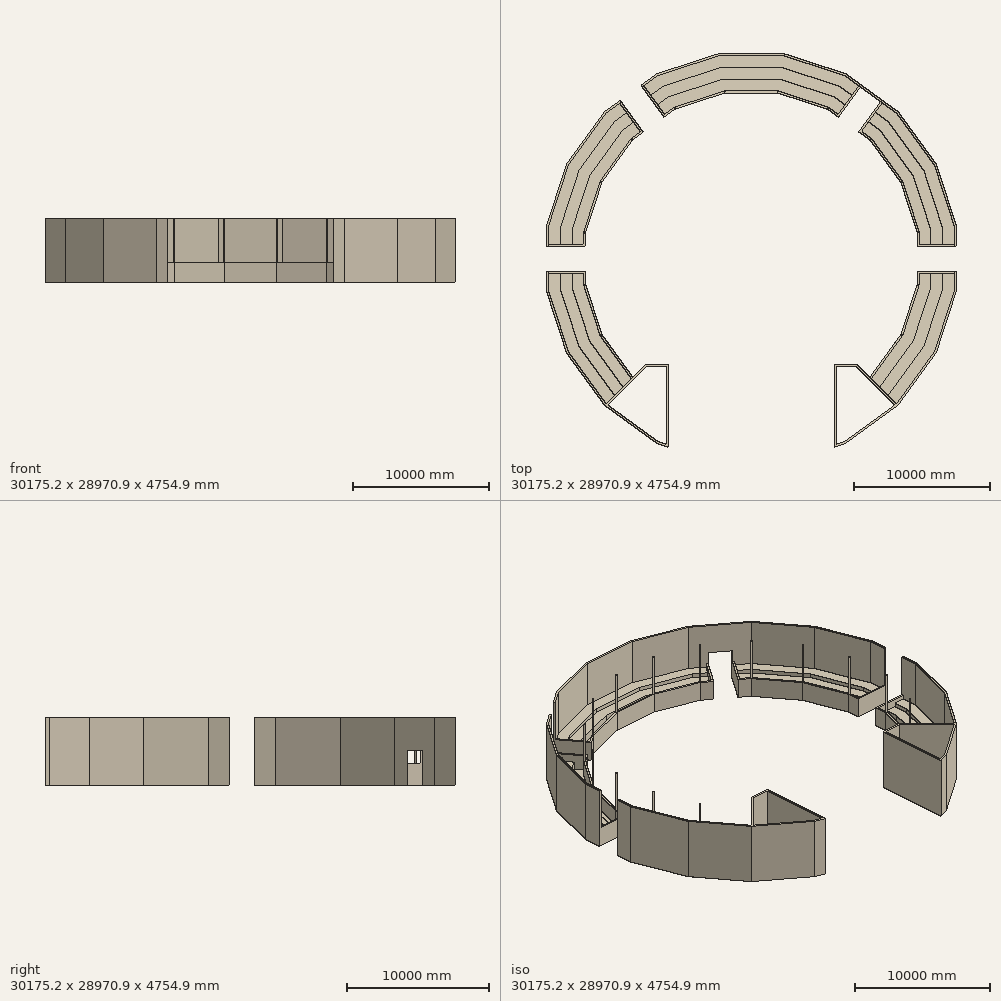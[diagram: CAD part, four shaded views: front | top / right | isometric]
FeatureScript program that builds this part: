
annotation { "Feature Type Name" : "Feature", "Feature Type Description" : "" }
export const myFeature = defineFeature(function(context is Context, id is Id, definition is map)
    precondition{}
    {
        {
            var Q0;
            Q0=qCreatedBy(makeId("Top.planeOp"),FACE);
            var sketch = newSketch(context, id + "F0", { "sketchPlane" : qUnion([Q0])});
            skLineSegment(sketch, "E0.0", {"start": v(-2389.64, 15087.6) * mm, "end": v(2389.64, 15087.6) * mm});
            skLineSegment(sketch, "E0.1", {"start": v(2389.64, 15087.6) * mm, "end": v(6935, 13610.72) * mm});
            skLineSegment(sketch, "E0.2", {"start": v(6935, 13610.72) * mm, "end": v(10801.53, 10801.53) * mm});
            skLineSegment(sketch, "E0.3", {"start": v(10801.53, 10801.53) * mm, "end": v(13610.72, 6935) * mm});
            skLineSegment(sketch, "E0.4", {"start": v(13610.72, 6935) * mm, "end": v(15087.6, 2389.64) * mm});
            skLineSegment(sketch, "E0.5", {"start": v(15087.6, 2389.64) * mm, "end": v(15087.6, -2389.64) * mm});
            skLineSegment(sketch, "E0.6", {"start": v(15087.6, -2389.64) * mm, "end": v(13610.72, -6935) * mm});
            skLineSegment(sketch, "E0.7", {"start": v(13610.72, -6935) * mm, "end": v(10801.53, -10801.53) * mm});
            skLineSegment(sketch, "E0.8", {"start": v(10801.53, -10801.53) * mm, "end": v(6935, -13610.72) * mm});
            skLineSegment(sketch, "E0.9", {"start": v(6935, -13610.72) * mm, "end": v(2389.64, -15087.6) * mm});
            skLineSegment(sketch, "E0.10", {"start": v(2389.64, -15087.6) * mm, "end": v(-2389.64, -15087.6) * mm});
            skLineSegment(sketch, "E0.11", {"start": v(-2389.64, -15087.6) * mm, "end": v(-6935, -13610.72) * mm});
            skLineSegment(sketch, "E0.12", {"start": v(-6935, -13610.72) * mm, "end": v(-10801.53, -10801.53) * mm});
            skLineSegment(sketch, "E0.13", {"start": v(-10801.53, -10801.53) * mm, "end": v(-13610.72, -6935) * mm});
            skLineSegment(sketch, "E0.14", {"start": v(-13610.72, -6935) * mm, "end": v(-15087.6, -2389.64) * mm});
            skLineSegment(sketch, "E0.15", {"start": v(-15087.6, -2389.64) * mm, "end": v(-15087.6, 2389.64) * mm});
            skLineSegment(sketch, "E0.16", {"start": v(-15087.6, 2389.64) * mm, "end": v(-13610.72, 6935) * mm});
            skLineSegment(sketch, "E0.17", {"start": v(-13610.72, 6935) * mm, "end": v(-10801.53, 10801.53) * mm});
            skLineSegment(sketch, "E0.18", {"start": v(-10801.53, 10801.53) * mm, "end": v(-6935, 13610.72) * mm});
            skLineSegment(sketch, "E0.19", {"start": v(-6935, 13610.72) * mm, "end": v(-2389.64, 15087.6) * mm});
            skLineSegment(sketch, "E1", {"start": v(-6705.6, -7772.4) * mm, "end": v(-6705.6, -152.4) * mm});
            skLineSegment(sketch, "E2", {"start": v(-6705.6, -152.4) * mm, "end": v(6705.6, -152.4) * mm});
            skLineSegment(sketch, "E3", {"start": v(6705.6, -152.4) * mm, "end": v(6705.6, -7772.4) * mm});
            skLineSegment(sketch, "E4", {"start": v(-6096, -7772.4) * mm, "end": v(-6096, -13883.33) * mm});
            skLineSegment(sketch, "E5", {"start": v(6096, -7772.4) * mm, "end": v(6096, -13883.33) * mm});
            skLineSegment(sketch, "E6", {"start": v(-7772.4, -7772.4) * mm, "end": v(-6096, -7772.4) * mm});
            skLineSegment(sketch, "E7", {"start": v(6096, -7772.4) * mm, "end": v(6705.6, -7772.4) * mm});
            skPoint(sketch, "E8.startSnap0", {"position": v(0, -15087.6) * mm});
            skLineSegment(sketch, "E9.0", {"start": v(-1931.02, 12192) * mm, "end": v(1931.02, 12192) * mm});
            skLineSegment(sketch, "E9.1", {"start": v(1931.02, 12192) * mm, "end": v(5604.05, 10998.56) * mm});
            skLineSegment(sketch, "E9.2", {"start": v(5604.05, 10998.56) * mm, "end": v(6426.51, 10401) * mm});
            skLineSegment(sketch, "E9.3", {"start": v(8728.5, 8728.5) * mm, "end": v(10998.56, 5604.05) * mm});
            skLineSegment(sketch, "E9.4", {"start": v(10998.56, 5604.05) * mm, "end": v(12192, 1931.02) * mm});
            skLineSegment(sketch, "E9.5", {"start": v(12192, 1931.02) * mm, "end": v(12192, 914.4) * mm});
            skLineSegment(sketch, "E9.6", {"start": v(12192, -1931.02) * mm, "end": v(10998.56, -5604.05) * mm});
            skLineSegment(sketch, "E9.13", {"start": v(-8728.5, -8728.5) * mm, "end": v(-10998.56, -5604.05) * mm});
            skLineSegment(sketch, "E9.14", {"start": v(-10998.56, -5604.05) * mm, "end": v(-12192, -1931.02) * mm});
            skLineSegment(sketch, "E9.15", {"start": v(-12192, -1931.02) * mm, "end": v(-12192, -914.4) * mm});
            skLineSegment(sketch, "E9.16", {"start": v(-12192, 1931.02) * mm, "end": v(-10998.56, 5604.05) * mm});
            skLineSegment(sketch, "E9.17", {"start": v(-10998.56, 5604.05) * mm, "end": v(-8728.5, 8728.5) * mm});
            skLineSegment(sketch, "E9.18", {"start": v(-8728.5, 8728.5) * mm, "end": v(-7953.14, 9291.85) * mm});
            skLineSegment(sketch, "E9.19", {"start": v(-5604.05, 10998.56) * mm, "end": v(-1931.02, 12192) * mm});
            skLineSegment(sketch, "E10", {"start": v(-15087.6, 0) * mm, "end": v(-15087.6, 914.4) * mm});
            skLineSegment(sketch, "E11", {"start": v(-14935.2, 914.4) * mm, "end": v(-12192, 914.4) * mm});
            skPoint(sketch, "E11.endSnap0", {"position": v(15087.6, 0) * mm});
            skLineSegment(sketch, "E12", {"start": v(15087.6, 914.4) * mm, "end": v(15087.6, -914.4) * mm});
            skLineSegment(sketch, "E13", {"start": v(14935.2, -914.4) * mm, "end": v(12192, -914.4) * mm});
            skLineSegment(sketch, "E14.trimOffspring", {"start": v(12192, 914.4) * mm, "end": v(14935.2, 914.4) * mm});
            skLineSegment(sketch, "E15.trimOffspring", {"start": v(-12192, -914.4) * mm, "end": v(-14935.2, -914.4) * mm});
            skLineSegment(sketch, "E16.trimOffspring", {"start": v(-12192, 914.4) * mm, "end": v(-12192, 1931.02) * mm});
            skLineSegment(sketch, "E17.trimOffspring", {"start": v(12192, -914.4) * mm, "end": v(12192, -1931.02) * mm});
            skLineSegment(sketch, "E18", {"start": v(-7953.14, 9291.85) * mm, "end": v(-9565.55, 11511.14) * mm});
            skLineSegment(sketch, "E19", {"start": v(-9655.13, 11634.44) * mm, "end": v(-8128.5, 12743.6) * mm});
            skLineSegment(sketch, "E20", {"start": v(-8038.93, 12620.3) * mm, "end": v(-6426.51, 10401) * mm});
            skLineSegment(sketch, "E21.trimOffspring", {"start": v(-6426.51, 10401) * mm, "end": v(-5604.05, 10998.56) * mm});
            skLineSegment(sketch, "E22.MirrorCS", {"start": v(8038.93, 12620.3) * mm, "end": v(6426.51, 10401) * mm});
            skLineSegment(sketch, "E23.MirrorCS", {"start": v(7906.04, 9326.06) * mm, "end": v(9518.46, 11545.36) * mm});
            skLineSegment(sketch, "E24.trimOffspring", {"start": v(7906.04, 9326.06) * mm, "end": v(8728.5, 8728.5) * mm});
            skLineSegment(sketch, "E25.0", {"start": v(-2365.5, 14935.2) * mm, "end": v(2365.5, 14935.2) * mm});
            skLineSegment(sketch, "E25.1", {"start": v(2365.5, 14935.2) * mm, "end": v(6864.96, 13473.24) * mm});
            skLineSegment(sketch, "E25.2", {"start": v(6864.96, 13473.24) * mm, "end": v(7915.63, 12709.88) * mm});
            skLineSegment(sketch, "E25.3", {"start": v(10692.42, 10692.42) * mm, "end": v(13473.24, 6864.96) * mm});
            skLineSegment(sketch, "E25.4", {"start": v(13473.24, 6864.96) * mm, "end": v(14935.2, 2365.5) * mm});
            skLineSegment(sketch, "E25.5", {"start": v(14935.2, 2365.5) * mm, "end": v(14935.2, 1066.8) * mm});
            skLineSegment(sketch, "E25.6", {"start": v(14935.2, -2365.5) * mm, "end": v(13473.24, -6864.96) * mm});
            skLineSegment(sketch, "E25.12", {"start": v(-6864.96, -13473.24) * mm, "end": v(-10567.6, -10783.12) * mm});
            skLineSegment(sketch, "E25.13", {"start": v(-10692.42, -10692.42) * mm, "end": v(-13473.24, -6864.96) * mm});
            skLineSegment(sketch, "E25.14", {"start": v(-13473.24, -6864.96) * mm, "end": v(-14935.2, -2365.5) * mm});
            skLineSegment(sketch, "E25.15", {"start": v(-14935.2, -2365.5) * mm, "end": v(-14935.2, -1066.8) * mm});
            skLineSegment(sketch, "E25.16", {"start": v(-14935.2, 2365.5) * mm, "end": v(-13473.24, 6864.96) * mm});
            skLineSegment(sketch, "E25.17", {"start": v(-13473.24, 6864.96) * mm, "end": v(-10692.42, 10692.42) * mm});
            skLineSegment(sketch, "E25.18", {"start": v(-10692.42, 10692.42) * mm, "end": v(-9688.84, 11421.57) * mm});
            skLineSegment(sketch, "E25.19", {"start": v(-6864.96, 13473.24) * mm, "end": v(-2365.5, 14935.2) * mm});
            skLineSegment(sketch, "E26.trimOffspring", {"start": v(-7915.63, 12709.88) * mm, "end": v(-6864.96, 13473.24) * mm});
            skLineSegment(sketch, "E27", {"start": v(0, 12192) * mm, "end": v(0, 12344.4) * mm});
            skLineSegment(sketch, "E28.0", {"start": v(-1955.16, 12344.4) * mm, "end": v(1955.16, 12344.4) * mm});
            skLineSegment(sketch, "E28.1", {"start": v(1955.16, 12344.4) * mm, "end": v(5674.1, 11136.04) * mm});
            skLineSegment(sketch, "E28.2", {"start": v(5674.1, 11136.04) * mm, "end": v(6392.8, 10613.88) * mm});
            skLineSegment(sketch, "E28.3", {"start": v(8837.61, 8837.61) * mm, "end": v(11136.04, 5674.1) * mm});
            skLineSegment(sketch, "E28.4", {"start": v(11136.04, 5674.1) * mm, "end": v(12344.4, 1955.16) * mm});
            skLineSegment(sketch, "E28.5", {"start": v(12344.4, 1955.16) * mm, "end": v(12344.4, 1066.8) * mm});
            skLineSegment(sketch, "E28.6", {"start": v(12344.4, -1955.16) * mm, "end": v(11136.04, -5674.1) * mm});
            skLineSegment(sketch, "E28.13", {"start": v(-8837.61, -8837.61) * mm, "end": v(-11136.04, -5674.1) * mm});
            skLineSegment(sketch, "E28.14", {"start": v(-11136.04, -5674.1) * mm, "end": v(-12344.4, -1955.16) * mm});
            skLineSegment(sketch, "E28.15", {"start": v(-12344.4, -1955.16) * mm, "end": v(-12344.4, -1066.8) * mm});
            skLineSegment(sketch, "E28.16", {"start": v(-12344.4, 1955.16) * mm, "end": v(-11136.04, 5674.1) * mm});
            skLineSegment(sketch, "E28.17", {"start": v(-11136.04, 5674.1) * mm, "end": v(-8837.61, 8837.61) * mm});
            skLineSegment(sketch, "E28.18", {"start": v(-8837.61, 8837.61) * mm, "end": v(-8166, 9325.56) * mm});
            skLineSegment(sketch, "E28.19", {"start": v(-5674.1, 11136.04) * mm, "end": v(-1955.16, 12344.4) * mm});
            skPoint(sketch, "E28.0.midPoint", {"position": v(0, 12344.4) * mm});
            skLineSegment(sketch, "E29.trimOffspring", {"start": v(-6392.8, 10613.88) * mm, "end": v(-5674.1, 11136.04) * mm});
            skLineSegment(sketch, "E30.trimOffspring", {"start": v(8118.92, 9359.78) * mm, "end": v(8837.61, 8837.61) * mm});
            skLineSegment(sketch, "E31", {"start": v(-10692.42, -10692.42) * mm, "end": v(-7772.4, -7772.4) * mm});
            skLineSegment(sketch, "E32", {"start": v(-8837.61, -8837.61) * mm, "end": v(-10692.42, -10692.42) * mm});
            skLineSegment(sketch, "E33", {"start": v(-7709.27, -7924.8) * mm, "end": v(-10567.6, -10783.12) * mm});
            skLineSegment(sketch, "E34", {"start": v(-6096, -7772.4) * mm, "end": v(-6096, -7924.8) * mm});
            skLineSegment(sketch, "E35", {"start": v(-6248.4, -7924.8) * mm, "end": v(-7709.27, -7924.8) * mm});
            skPoint(sketch, "E36.orphan", {"position": v(-7556.87, -7772.4) * mm});
            skLineSegment(sketch, "E37", {"start": v(-6248.4, -7924.8) * mm, "end": v(-6248.4, -13673.57) * mm});
            skLineSegment(sketch, "E38.trimOffspring", {"start": v(-6248.4, -13673.57) * mm, "end": v(-6864.96, -13473.24) * mm});
            skLineSegment(sketch, "E39.MirrorCS", {"start": v(8728.5, -8728.5) * mm, "end": v(10998.56, -5604.05) * mm});
            skLineSegment(sketch, "E40.MirrorCS", {"start": v(7709.27, -7924.8) * mm, "end": v(10567.6, -10783.12) * mm});
            skLineSegment(sketch, "E41.MirrorCS", {"start": v(6248.4, -7924.8) * mm, "end": v(7709.27, -7924.8) * mm});
            skLineSegment(sketch, "E42.MirrorCS", {"start": v(7772.4, -7772.4) * mm, "end": v(6096, -7772.4) * mm});
            skPoint(sketch, "E43.MirrorP", {"position": v(7556.87, -7772.4) * mm});
            skLineSegment(sketch, "E44.MirrorCS", {"start": v(8837.61, -8837.61) * mm, "end": v(11136.04, -5674.1) * mm});
            skLineSegment(sketch, "E45.MirrorCS", {"start": v(10692.42, -10692.42) * mm, "end": v(7772.4, -7772.4) * mm});
            skLineSegment(sketch, "E46.MirrorCS", {"start": v(8837.61, -8837.61) * mm, "end": v(10692.42, -10692.42) * mm});
            skLineSegment(sketch, "E47.MirrorCS", {"start": v(6864.96, -13473.24) * mm, "end": v(10567.6, -10783.12) * mm});
            skLineSegment(sketch, "E48.MirrorCS", {"start": v(10692.42, -10692.42) * mm, "end": v(13473.24, -6864.96) * mm});
            skLineSegment(sketch, "E49.MirrorCS", {"start": v(6248.4, -13673.57) * mm, "end": v(6864.96, -13473.24) * mm});
            skLineSegment(sketch, "E50.MirrorCS", {"start": v(6248.4, -7924.8) * mm, "end": v(6248.4, -13673.57) * mm});
            skLineSegment(sketch, "E51.trimOffspring", {"start": v(-12344.4, 1066.8) * mm, "end": v(-12344.4, 1955.16) * mm});
            skLineSegment(sketch, "E52.trimOffspring", {"start": v(-14935.2, 1066.8) * mm, "end": v(-14935.2, 2365.5) * mm});
            skLineSegment(sketch, "E53", {"start": v(-14935.2, -1066.8) * mm, "end": v(-12344.4, -1066.8) * mm});
            skLineSegment(sketch, "E54.0", {"start": v(-14071.6, -2228.72) * mm, "end": v(-14071.6, -1066.8) * mm});
            skLineSegment(sketch, "E54.1", {"start": v(-14071.6, 2228.72) * mm, "end": v(-12694.17, 6468) * mm});
            skLineSegment(sketch, "E54.2", {"start": v(-12694.17, 6468) * mm, "end": v(-10074.15, 10074.15) * mm});
            skLineSegment(sketch, "E54.3", {"start": v(-10074.15, 10074.15) * mm, "end": v(-9181.23, 10722.9) * mm});
            skLineSegment(sketch, "E54.4", {"start": v(-6468, 12694.17) * mm, "end": v(-2228.72, 14071.6) * mm});
            skLineSegment(sketch, "E54.5", {"start": v(-2228.72, 14071.6) * mm, "end": v(2228.72, 14071.6) * mm});
            skLineSegment(sketch, "E54.6", {"start": v(2228.72, 14071.6) * mm, "end": v(6468, 12694.17) * mm});
            skLineSegment(sketch, "E54.7", {"start": v(6468, 12694.17) * mm, "end": v(7408.02, 12011.21) * mm});
            skLineSegment(sketch, "E54.8", {"start": v(10074.15, 10074.15) * mm, "end": v(12694.17, 6468) * mm});
            skLineSegment(sketch, "E54.9", {"start": v(12694.17, 6468) * mm, "end": v(14071.6, 2228.72) * mm});
            skLineSegment(sketch, "E54.10", {"start": v(14071.6, 2228.72) * mm, "end": v(14071.6, 1066.8) * mm});
            skLineSegment(sketch, "E54.11", {"start": v(14071.6, -2228.72) * mm, "end": v(12694.17, -6468) * mm});
            skLineSegment(sketch, "E54.12", {"start": v(12694.17, -6468) * mm, "end": v(10074.15, -10074.15) * mm});
            skLineSegment(sketch, "E54.18", {"start": v(-10074.15, -10074.15) * mm, "end": v(-12694.17, -6468) * mm});
            skLineSegment(sketch, "E54.19", {"start": v(-12694.17, -6468) * mm, "end": v(-14071.6, -2228.72) * mm});
            skLineSegment(sketch, "E55.0", {"start": v(-13208, -2091.94) * mm, "end": v(-13208, -1066.8) * mm});
            skLineSegment(sketch, "E55.1", {"start": v(-13208, 2091.94) * mm, "end": v(-11915.1, 6071.05) * mm});
            skLineSegment(sketch, "E55.2", {"start": v(-11915.1, 6071.05) * mm, "end": v(-9455.88, 9455.88) * mm});
            skLineSegment(sketch, "E55.3", {"start": v(-9455.88, 9455.88) * mm, "end": v(-8673.62, 10024.23) * mm});
            skLineSegment(sketch, "E55.4", {"start": v(-6071.05, 11915.1) * mm, "end": v(-2091.94, 13208) * mm});
            skLineSegment(sketch, "E55.5", {"start": v(-2091.94, 13208) * mm, "end": v(2091.94, 13208) * mm});
            skLineSegment(sketch, "E55.6", {"start": v(2091.94, 13208) * mm, "end": v(6071.05, 11915.1) * mm});
            skLineSegment(sketch, "E55.8", {"start": v(9455.88, 9455.88) * mm, "end": v(11915.1, 6071.05) * mm});
            skLineSegment(sketch, "E55.9", {"start": v(11915.1, 6071.05) * mm, "end": v(13208, 2091.94) * mm});
            skLineSegment(sketch, "E55.10", {"start": v(13208, 2091.94) * mm, "end": v(13208, 1066.8) * mm});
            skLineSegment(sketch, "E55.11", {"start": v(13208, -2091.94) * mm, "end": v(11915.1, -6071.05) * mm});
            skLineSegment(sketch, "E55.12", {"start": v(11915.1, -6071.05) * mm, "end": v(9455.88, -9455.88) * mm});
            skLineSegment(sketch, "E55.18", {"start": v(-9455.88, -9455.88) * mm, "end": v(-11915.1, -6071.05) * mm});
            skLineSegment(sketch, "E55.19", {"start": v(-11915.1, -6071.05) * mm, "end": v(-13208, -2091.94) * mm});
            skLineSegment(sketch, "E56.trimOffspring", {"start": v(-14071.6, 1066.8) * mm, "end": v(-14071.6, 2228.72) * mm});
            skLineSegment(sketch, "E57", {"start": v(-13208, 2091.94) * mm, "end": v(-13208, 1066.8) * mm});
            skLineSegment(sketch, "E58", {"start": v(-14935.2, 1066.8) * mm, "end": v(-12344.4, 1066.8) * mm});
            skLineSegment(sketch, "E59", {"start": v(-9688.84, 11421.57) * mm, "end": v(-8166, 9325.56) * mm});
            skLineSegment(sketch, "E60", {"start": v(-7915.63, 12709.88) * mm, "end": v(-6392.8, 10613.88) * mm});
            skLineSegment(sketch, "E61.trimOffspring", {"start": v(-7408.02, 12011.21) * mm, "end": v(-6468, 12694.17) * mm});
            skLineSegment(sketch, "E62.trimOffspring", {"start": v(-6900.4, 11312.55) * mm, "end": v(-6071.05, 11915.1) * mm});
            skLineSegment(sketch, "E63", {"start": v(6392.8, 10613.88) * mm, "end": v(7915.63, 12709.88) * mm});
            skLineSegment(sketch, "E64.trimOffspring", {"start": v(9134.14, 10757.11) * mm, "end": v(10074.15, 10074.15) * mm});
            skLineSegment(sketch, "E65.trimOffspring", {"start": v(8626.53, 10058.45) * mm, "end": v(9455.88, 9455.88) * mm});
            skLineSegment(sketch, "E66.trimOffspring", {"start": v(9641.75, 11455.78) * mm, "end": v(10692.42, 10692.42) * mm});
            skLineSegment(sketch, "E67", {"start": v(8118.92, 9359.78) * mm, "end": v(9641.75, 11455.78) * mm});
            skLineSegment(sketch, "E68", {"start": v(6071.05, 11915.1) * mm, "end": v(6900.4, 11312.55) * mm});
            skLineSegment(sketch, "E69.trimOffspring", {"start": v(12344.4, -1066.8) * mm, "end": v(12344.4, -1955.16) * mm});
            skLineSegment(sketch, "E70.trimOffspring", {"start": v(13208, -1066.8) * mm, "end": v(13208, -2091.94) * mm});
            skLineSegment(sketch, "E71.trimOffspring", {"start": v(14071.6, -1066.8) * mm, "end": v(14071.6, -2228.72) * mm});
            skLineSegment(sketch, "E72", {"start": v(12344.4, 1066.8) * mm, "end": v(14935.2, 1066.8) * mm});
            skLineSegment(sketch, "E73", {"start": v(12344.4, -1066.8) * mm, "end": v(14935.2, -1066.8) * mm});
            skLineSegment(sketch, "E74.trimOffspring", {"start": v(14935.2, -1066.8) * mm, "end": v(14935.2, -2365.5) * mm});
            skLineSegment(sketch, "E75", {"start": v(-8038.93, 12620.3) * mm, "end": v(-9565.55, 11511.14) * mm});
            skLineSegment(sketch, "E76", {"start": v(8038.93, 12620.3) * mm, "end": v(9518.46, 11545.36) * mm});
            skLineSegment(sketch, "E77", {"start": v(14935.2, -914.4) * mm, "end": v(14935.2, 914.4) * mm});
            skLineSegment(sketch, "E78", {"start": v(-14935.2, 914.4) * mm, "end": v(-14935.2, -914.4) * mm});
            skLineSegment(sketch, "E79", {"start": v(-14935.2, -914.4) * mm, "end": v(-14935.2, -1066.8) * mm});
            skLineSegment(sketch, "E80", {"start": v(-14935.2, 1066.8) * mm, "end": v(-14935.2, 914.4) * mm});
            skLineSegment(sketch, "E81", {"start": v(-9565.55, 11511.14) * mm, "end": v(-9688.84, 11421.57) * mm});
            skLineSegment(sketch, "E82", {"start": v(-8038.93, 12620.3) * mm, "end": v(-7915.63, 12709.88) * mm});
            skLineSegment(sketch, "E83", {"start": v(7915.63, 12709.88) * mm, "end": v(8038.93, 12620.3) * mm});
            skLineSegment(sketch, "E84", {"start": v(9518.46, 11545.36) * mm, "end": v(9641.75, 11455.78) * mm});
            skLineSegment(sketch, "E85", {"start": v(14935.2, -914.4) * mm, "end": v(14935.2, -1066.8) * mm});
            skLineSegment(sketch, "E86", {"start": v(14935.2, 1066.8) * mm, "end": v(14935.2, 914.4) * mm});
            skPoint(sketch, "E87.center", {"position": v(0, 0) * mm});
            skCircle(sketch, "E88", {"center": v(-11067.3, -5639.07) * mm, "radius": 60.96 * mm});
            skCircle(sketch, "E89.7.0", {"center": v(11067.3, -5639.07) * mm, "radius": 60.96 * mm});
            skCircle(sketch, "E89.8.0", {"center": v(12268.2, -1943.1) * mm, "radius": 60.96 * mm});
            skCircle(sketch, "E89.9.0", {"center": v(12268.2, 1943.1) * mm, "radius": 60.96 * mm});
            skCircle(sketch, "E89.10.0", {"center": v(11067.3, 5639.07) * mm, "radius": 60.96 * mm});
            skCircle(sketch, "E89.11.0", {"center": v(8783.06, 8783.06) * mm, "radius": 60.96 * mm});
            skCircle(sketch, "E89.12.0", {"center": v(5639.07, 11067.3) * mm, "radius": 60.96 * mm});
            skCircle(sketch, "E89.13.0", {"center": v(1943.1, 12268.2) * mm, "radius": 60.96 * mm});
            skCircle(sketch, "E89.14.0", {"center": v(-1943.1, 12268.2) * mm, "radius": 60.96 * mm});
            skCircle(sketch, "E89.15.0", {"center": v(-5639.07, 11067.3) * mm, "radius": 60.96 * mm});
            skCircle(sketch, "E89.16.0", {"center": v(-8783.06, 8783.06) * mm, "radius": 60.96 * mm});
            skCircle(sketch, "E89.17.0", {"center": v(-11067.3, 5639.07) * mm, "radius": 60.96 * mm});
            skCircle(sketch, "E89.18.0", {"center": v(-12268.2, 1943.1) * mm, "radius": 60.96 * mm});
            skCircle(sketch, "E89.19.0", {"center": v(-12268.2, -1943.1) * mm, "radius": 60.96 * mm});
            skLineSegment(sketch, "E90", {"start": v(-9565.55, 11511.14) * mm, "end": v(-9655.13, 11634.44) * mm});
            skLineSegment(sketch, "E91", {"start": v(-8038.93, 12620.3) * mm, "end": v(-8128.5, 12743.6) * mm});
            skLineSegment(sketch, "E92", {"start": v(-14935.2, -914.4) * mm, "end": v(-15087.6, -914.4) * mm});
            skLineSegment(sketch, "E93", {"start": v(-14935.2, 914.4) * mm, "end": v(-15087.6, 914.4) * mm});
            skLineSegment(sketch, "E94", {"start": v(14935.2, 914.4) * mm, "end": v(15087.6, 914.4) * mm});
            skLineSegment(sketch, "E95", {"start": v(14935.2, -914.4) * mm, "end": v(15087.6, -914.4) * mm});
            skLineSegment(sketch, "E96", {"start": v(8038.93, 12620.3) * mm, "end": v(8128.5, 12743.6) * mm});
            skLineSegment(sketch, "E97", {"start": v(9518.46, 11545.36) * mm, "end": v(9608.03, 11668.65) * mm});
            skSolve(sketch);
        }
        {
            var Q0;
            Q0=makeQuery(id+"F0.imprint","IMPRINT",FACE,{"disambiguationData":[TD([[makeQuery(id+"F0.imprint","IMPRINT",EDGE,{"derivedFrom":sQuery(id+"F0.wireOp",EDGE,"E0.0")}),-1.0]])]});
            var Q1;
            {var subQ8=sQuery(id+"F0.wireOp",EDGE,"E0.12");Q1=makeQuery(id+"F0.imprint","IMPRINT",FACE,{"disambiguationData":[TD([[makeQuery(id+"F0.imprint","IMPRINT",EDGE,{"derivedFrom":subQ8}),-1.0]])]});}
            var Q2;
            {var subQ1=sQuery(id+"F0.wireOp",EDGE,"E10");Q2=makeQuery(id+"F0.imprint","IMPRINT",FACE,{"disambiguationData":[TD([[makeQuery(id+"F0.imprint","IMPRINT",EDGE,{"derivedFrom":subQ1}),-1.0]])]});}
            var Q3;
            {var subQ2=sQuery(id+"F0.wireOp",EDGE,"E0.16");Q3=makeQuery(id+"F0.imprint","IMPRINT",FACE,{"disambiguationData":[TD([[makeQuery(id+"F0.imprint","IMPRINT",EDGE,{"derivedFrom":subQ2}),-1.0]])]});}
            var Q4;
            Q4=makeQuery(id+"F0.imprint","IMPRINT",FACE,{"disambiguationData":[TD([[makeQuery(id+"F0.imprint","IMPRINT",EDGE,{"derivedFrom":sQuery(id+"F0.wireOp",EDGE,"E19")}),-1.0]])]});
            var Q5;
            Q5=makeQuery(id+"F0.imprint","IMPRINT",FACE,{"disambiguationData":[TD([[makeQuery(id+"F0.imprint","IMPRINT",EDGE,{"derivedFrom":sQuery(id+"F0.wireOp",EDGE,"E76")}),1.0]])]});
            var Q6;
            {var subQ0=sQuery(id+"F0.wireOp",EDGE,"E0.3");Q6=makeQuery(id+"F0.imprint","IMPRINT",FACE,{"disambiguationData":[TD([[makeQuery(id+"F0.imprint","IMPRINT",EDGE,{"derivedFrom":subQ0}),-1.0]])]});}
            var Q7;
            Q7=makeQuery(id+"F0.imprint","IMPRINT",FACE,{"disambiguationData":[TD([[makeQuery(id+"F0.imprint","IMPRINT",EDGE,{"derivedFrom":sQuery(id+"F0.wireOp",EDGE,"E12")}),-1.0]])]});
            var Q8;
            {var subQ12=sQuery(id+"F0.wireOp",EDGE,"E0.6");Q8=makeQuery(id+"F0.imprint","IMPRINT",FACE,{"disambiguationData":[TD([[makeQuery(id+"F0.imprint","IMPRINT",EDGE,{"derivedFrom":subQ12}),-1.0]])]});}
            extrude(context, id + "F1", {"entities" : qUnion([Q0, Q1, Q2, Q3, Q4, Q5, Q6, Q7, Q8]), "depth" : 4754.88 * mm, "offsetDistance" : 30.48 * mm});
        }
        {
            var Q0;
            Q0=makeQuery(id+"F0.imprint","IMPRINT",FACE,{"disambiguationData":[TD([[makeQuery(id+"F0.imprint","IMPRINT",EDGE,{"derivedFrom":sQuery(id+"F0.wireOp",EDGE,"E9.16")}),1.0]])]});
            var Q1;
            {var subQ6=sQuery(id+"F0.wireOp",EDGE,"E9.19");Q1=makeQuery(id+"F0.imprint","IMPRINT",FACE,{"disambiguationData":[TD([[makeQuery(id+"F0.imprint","IMPRINT",EDGE,{"derivedFrom":subQ6}),1.0]])]});}
            var Q2;
            {var subQ6=sQuery(id+"F0.wireOp",EDGE,"E9.1");Q2=makeQuery(id+"F0.imprint","IMPRINT",FACE,{"disambiguationData":[TD([[makeQuery(id+"F0.imprint","IMPRINT",EDGE,{"derivedFrom":subQ6}),1.0]])]});}
            var Q3;
            Q3=makeQuery(id+"F0.imprint","IMPRINT",FACE,{"disambiguationData":[TD([[makeQuery(id+"F0.imprint","IMPRINT",EDGE,{"derivedFrom":sQuery(id+"F0.wireOp",EDGE,"E9.3")}),1.0]])]});
            var Q4;
            {var subQ6=sQuery(id+"F0.wireOp",EDGE,"E9.13");Q4=makeQuery(id+"F0.imprint","IMPRINT",FACE,{"disambiguationData":[TD([[makeQuery(id+"F0.imprint","IMPRINT",EDGE,{"derivedFrom":subQ6}),1.0]])]});}
            var Q5;
            Q5=makeQuery(id+"F0.imprint","IMPRINT",FACE,{"disambiguationData":[TD([[makeQuery(id+"F0.imprint","IMPRINT",EDGE,{"derivedFrom":sQuery(id+"F0.wireOp",EDGE,"E9.6")}),1.0]])]});
            var Q6;
            {var subQ0=sQuery(id+"F0.wireOp",EDGE,"E9.14");Q6=makeQuery(id+"F0.imprint","IMPRINT",FACE,{"disambiguationData":[TD([[makeQuery(id+"F0.imprint","IMPRINT",EDGE,{"derivedFrom":subQ0}),1.0]])]});}
            var Q7;
            {var subQ0=sQuery(id+"F0.wireOp",EDGE,"yEdqs7aw-UTsJ-shgV-JAjx-2IsReYrC0puD");var subQ2=sQuery(id+"F0.wireOp",EDGE,"E28.13");var subQ4=makeQuery(id+"F0.imprint","INTERSECT",VERTEX,{"derivedFrom":[subQ2,subQ0]});Q7=makeQuery(id+"F0.imprint","IMPRINT",FACE,{"disambiguationData":[TD([[makeQuery(id+"F0.imprint","IMPRINT",EDGE,{"disambiguationData":[TD([[subQ4,-1.0]])],"derivedFrom":subQ2}),-1.0]])]});}
            var Q8;
            {var subQ8=sQuery(id+"F0.wireOp",EDGE,"E9.15");Q8=makeQuery(id+"F0.imprint","IMPRINT",FACE,{"disambiguationData":[TD([[makeQuery(id+"F0.imprint","IMPRINT",EDGE,{"derivedFrom":subQ8}),1.0]])]});}
            var Q9;
            Q9=makeQuery(id+"F0.imprint","IMPRINT",FACE,{"disambiguationData":[TD([[makeQuery(id+"F0.imprint","IMPRINT",EDGE,{"derivedFrom":sQuery(id+"F0.wireOp",EDGE,"E11")}),1.0]])]});
            var Q10;
            {var subQ0=sQuery(id+"F0.wireOp",EDGE,"E87.19.0");var subQ2=sQuery(id+"F0.wireOp",EDGE,"E28.14");var subQ4=makeQuery(id+"F0.imprint","INTERSECT",VERTEX,{"derivedFrom":[subQ2,subQ0]});Q10=makeQuery(id+"F0.imprint","IMPRINT",FACE,{"disambiguationData":[TD([[makeQuery(id+"F0.imprint","IMPRINT",EDGE,{"disambiguationData":[TD([[subQ4,-1.0]])],"derivedFrom":subQ2}),-1.0]])]});}
            var Q11;
            {var subQ0=sQuery(id+"F0.wireOp",EDGE,"E87.18.0");var subQ2=sQuery(id+"F0.wireOp",EDGE,"E28.16");var subQ4=makeQuery(id+"F0.imprint","INTERSECT",VERTEX,{"derivedFrom":[subQ2,subQ0]});Q11=makeQuery(id+"F0.imprint","IMPRINT",FACE,{"disambiguationData":[TD([[makeQuery(id+"F0.imprint","IMPRINT",EDGE,{"disambiguationData":[TD([[subQ4,1.0]])],"derivedFrom":subQ2}),-1.0]])]});}
            var Q12;
            {var subQ0=sQuery(id+"F0.wireOp",EDGE,"E87.17.0");var subQ2=sQuery(id+"F0.wireOp",EDGE,"E28.16");var subQ4=makeQuery(id+"F0.imprint","INTERSECT",VERTEX,{"derivedFrom":[subQ2,subQ0]});Q12=makeQuery(id+"F0.imprint","IMPRINT",FACE,{"disambiguationData":[TD([[makeQuery(id+"F0.imprint","IMPRINT",EDGE,{"disambiguationData":[TD([[subQ4,-1.0]])],"derivedFrom":subQ2}),-1.0]])]});}
            var Q13;
            {var subQ0=sQuery(id+"F0.wireOp",EDGE,"E9.17");Q13=makeQuery(id+"F0.imprint","IMPRINT",FACE,{"disambiguationData":[TD([[makeQuery(id+"F0.imprint","IMPRINT",EDGE,{"derivedFrom":subQ0}),1.0]])]});}
            var Q14;
            {var subQ7=sQuery(id+"F0.wireOp",EDGE,"E9.18");Q14=makeQuery(id+"F0.imprint","IMPRINT",FACE,{"disambiguationData":[TD([[makeQuery(id+"F0.imprint","IMPRINT",EDGE,{"derivedFrom":subQ7}),1.0]])]});}
            var Q15;
            {var subQ0=sQuery(id+"F0.wireOp",EDGE,"E87.16.0");var subQ2=sQuery(id+"F0.wireOp",EDGE,"E28.17");var subQ4=makeQuery(id+"F0.imprint","INTERSECT",VERTEX,{"derivedFrom":[subQ2,subQ0]});Q15=makeQuery(id+"F0.imprint","IMPRINT",FACE,{"disambiguationData":[TD([[makeQuery(id+"F0.imprint","IMPRINT",EDGE,{"disambiguationData":[TD([[subQ4,-1.0]])],"derivedFrom":subQ2}),-1.0]])]});}
            var Q16;
            Q16=makeQuery(id+"F0.imprint","IMPRINT",FACE,{"disambiguationData":[TD([[makeQuery(id+"F0.imprint","IMPRINT",EDGE,{"derivedFrom":sQuery(id+"F0.wireOp",EDGE,"E20")}),1.0]])]});
            var Q17;
            {var subQ0=sQuery(id+"F0.wireOp",EDGE,"E87.15.0");var subQ2=sQuery(id+"F0.wireOp",EDGE,"E28.19");var subQ4=makeQuery(id+"F0.imprint","INTERSECT",VERTEX,{"derivedFrom":[subQ2,subQ0]});Q17=makeQuery(id+"F0.imprint","IMPRINT",FACE,{"disambiguationData":[TD([[makeQuery(id+"F0.imprint","IMPRINT",EDGE,{"disambiguationData":[TD([[subQ4,1.0]])],"derivedFrom":subQ2}),-1.0]])]});}
            var Q18;
            {var subQ0=sQuery(id+"F0.wireOp",EDGE,"E87.14.0");var subQ2=sQuery(id+"F0.wireOp",EDGE,"E28.0");var subQ4=makeQuery(id+"F0.imprint","INTERSECT",VERTEX,{"derivedFrom":[subQ2,subQ0]});Q18=makeQuery(id+"F0.imprint","IMPRINT",FACE,{"disambiguationData":[TD([[makeQuery(id+"F0.imprint","IMPRINT",EDGE,{"disambiguationData":[TD([[subQ4,1.0]])],"derivedFrom":subQ2}),-1.0]])]});}
            var Q19;
            {var subQ3=sQuery(id+"F0.wireOp",EDGE,"E27");Q19=makeQuery(id+"F0.imprint","IMPRINT",FACE,{"disambiguationData":[TD([[makeQuery(id+"F0.imprint","IMPRINT",EDGE,{"derivedFrom":subQ3}),1.0]])]});}
            var Q20;
            {var subQ3=sQuery(id+"F0.wireOp",EDGE,"E27");Q20=makeQuery(id+"F0.imprint","IMPRINT",FACE,{"disambiguationData":[TD([[makeQuery(id+"F0.imprint","IMPRINT",EDGE,{"derivedFrom":subQ3}),-1.0]])]});}
            var Q21;
            {var subQ0=sQuery(id+"F0.wireOp",EDGE,"E87.13.0");var subQ2=sQuery(id+"F0.wireOp",EDGE,"E28.0");var subQ4=makeQuery(id+"F0.imprint","INTERSECT",VERTEX,{"derivedFrom":[subQ2,subQ0]});Q21=makeQuery(id+"F0.imprint","IMPRINT",FACE,{"disambiguationData":[TD([[makeQuery(id+"F0.imprint","IMPRINT",EDGE,{"disambiguationData":[TD([[subQ4,-1.0]])],"derivedFrom":subQ2}),-1.0]])]});}
            var Q22;
            {var subQ7=sQuery(id+"F0.wireOp",EDGE,"E9.2");Q22=makeQuery(id+"F0.imprint","IMPRINT",FACE,{"disambiguationData":[TD([[makeQuery(id+"F0.imprint","IMPRINT",EDGE,{"derivedFrom":subQ7}),1.0]])]});}
            var Q23;
            {var subQ0=sQuery(id+"F0.wireOp",EDGE,"E87.12.0");var subQ2=sQuery(id+"F0.wireOp",EDGE,"E28.1");var subQ4=makeQuery(id+"F0.imprint","INTERSECT",VERTEX,{"derivedFrom":[subQ2,subQ0]});Q23=makeQuery(id+"F0.imprint","IMPRINT",FACE,{"disambiguationData":[TD([[makeQuery(id+"F0.imprint","IMPRINT",EDGE,{"disambiguationData":[TD([[subQ4,-1.0]])],"derivedFrom":subQ2}),-1.0]])]});}
            var Q24;
            Q24=makeQuery(id+"F0.imprint","IMPRINT",FACE,{"disambiguationData":[TD([[makeQuery(id+"F0.imprint","IMPRINT",EDGE,{"derivedFrom":sQuery(id+"F0.wireOp",EDGE,"E23.MirrorCS")}),-1.0]])]});
            var Q25;
            {var subQ0=sQuery(id+"F0.wireOp",EDGE,"E87.11.0");var subQ2=sQuery(id+"F0.wireOp",EDGE,"E28.3");var subQ4=makeQuery(id+"F0.imprint","INTERSECT",VERTEX,{"derivedFrom":[subQ2,subQ0]});Q25=makeQuery(id+"F0.imprint","IMPRINT",FACE,{"disambiguationData":[TD([[makeQuery(id+"F0.imprint","IMPRINT",EDGE,{"disambiguationData":[TD([[subQ4,1.0]])],"derivedFrom":subQ2}),-1.0]])]});}
            var Q26;
            {var subQ0=sQuery(id+"F0.wireOp",EDGE,"E87.10.0");var subQ2=sQuery(id+"F0.wireOp",EDGE,"E28.3");var subQ4=makeQuery(id+"F0.imprint","INTERSECT",VERTEX,{"derivedFrom":[subQ2,subQ0]});Q26=makeQuery(id+"F0.imprint","IMPRINT",FACE,{"disambiguationData":[TD([[makeQuery(id+"F0.imprint","IMPRINT",EDGE,{"disambiguationData":[TD([[subQ4,-1.0]])],"derivedFrom":subQ2}),-1.0]])]});}
            var Q27;
            {var subQ0=sQuery(id+"F0.wireOp",EDGE,"E9.4");Q27=makeQuery(id+"F0.imprint","IMPRINT",FACE,{"disambiguationData":[TD([[makeQuery(id+"F0.imprint","IMPRINT",EDGE,{"derivedFrom":subQ0}),1.0]])]});}
            var Q28;
            {var subQ0=sQuery(id+"F0.wireOp",EDGE,"E87.9.0");var subQ2=sQuery(id+"F0.wireOp",EDGE,"E28.4");var subQ4=makeQuery(id+"F0.imprint","INTERSECT",VERTEX,{"derivedFrom":[subQ2,subQ0]});Q28=makeQuery(id+"F0.imprint","IMPRINT",FACE,{"disambiguationData":[TD([[makeQuery(id+"F0.imprint","IMPRINT",EDGE,{"disambiguationData":[TD([[subQ4,-1.0]])],"derivedFrom":subQ2}),-1.0]])]});}
            var Q29;
            {var subQ7=sQuery(id+"F0.wireOp",EDGE,"E9.5");Q29=makeQuery(id+"F0.imprint","IMPRINT",FACE,{"disambiguationData":[TD([[makeQuery(id+"F0.imprint","IMPRINT",EDGE,{"derivedFrom":subQ7}),1.0]])]});}
            var Q30;
            Q30=makeQuery(id+"F0.imprint","IMPRINT",FACE,{"disambiguationData":[TD([[makeQuery(id+"F0.imprint","IMPRINT",EDGE,{"derivedFrom":sQuery(id+"F0.wireOp",EDGE,"E13")}),1.0]])]});
            var Q31;
            {var subQ0=sQuery(id+"F0.wireOp",EDGE,"E87.8.0");var subQ2=sQuery(id+"F0.wireOp",EDGE,"E28.6");var subQ4=makeQuery(id+"F0.imprint","INTERSECT",VERTEX,{"derivedFrom":[subQ2,subQ0]});Q31=makeQuery(id+"F0.imprint","IMPRINT",FACE,{"disambiguationData":[TD([[makeQuery(id+"F0.imprint","IMPRINT",EDGE,{"disambiguationData":[TD([[subQ4,1.0]])],"derivedFrom":subQ2}),-1.0]])]});}
            var Q32;
            {var subQ0=sQuery(id+"F0.wireOp",EDGE,"E87.7.0");var subQ2=sQuery(id+"F0.wireOp",EDGE,"E28.6");var subQ4=makeQuery(id+"F0.imprint","INTERSECT",VERTEX,{"derivedFrom":[subQ2,subQ0]});Q32=makeQuery(id+"F0.imprint","IMPRINT",FACE,{"disambiguationData":[TD([[makeQuery(id+"F0.imprint","IMPRINT",EDGE,{"disambiguationData":[TD([[subQ4,-1.0]])],"derivedFrom":subQ2}),-1.0]])]});}
            var Q33;
            {var subQ0=sQuery(id+"F0.wireOp",EDGE,"E39.MirrorCS");Q33=makeQuery(id+"F0.imprint","IMPRINT",FACE,{"disambiguationData":[TD([[makeQuery(id+"F0.imprint","IMPRINT",EDGE,{"derivedFrom":subQ0}),-1.0]])]});}
            extrude(context, id + "F2", {"entities" : qUnion([Q0, Q1, Q2, Q3, Q4, Q5, Q6, Q7, Q8, Q9, Q10, Q11, Q12, Q13, Q14, Q15, Q16, Q17, Q18, Q19, Q20, Q21, Q22, Q23, Q24, Q25, Q26, Q27, Q28, Q29, Q30, Q31, Q32, Q33]), "depth" : 1524 * mm, "offsetDistance" : 30.48 * mm});
        }
        {
            var Q0;
            {var subQ0=sQuery(id+"F0.wireOp",EDGE,"E54.0");Q0=makeQuery(id+"F0.imprint","IMPRINT",FACE,{"disambiguationData":[TD([[makeQuery(id+"F0.imprint","IMPRINT",EDGE,{"derivedFrom":subQ0}),-1.0]])]});}
            var Q1;
            Q1=makeQuery(id+"F0.imprint","IMPRINT",FACE,{"disambiguationData":[TD([[makeQuery(id+"F0.imprint","IMPRINT",EDGE,{"derivedFrom":sQuery(id+"F0.wireOp",EDGE,"E54.1")}),-1.0]])]});
            var Q2;
            Q2=makeQuery(id+"F0.imprint","IMPRINT",FACE,{"disambiguationData":[TD([[makeQuery(id+"F0.imprint","IMPRINT",EDGE,{"derivedFrom":sQuery(id+"F0.wireOp",EDGE,"E54.4")}),-1.0]])]});
            var Q3;
            Q3=makeQuery(id+"F0.imprint","IMPRINT",FACE,{"disambiguationData":[TD([[makeQuery(id+"F0.imprint","IMPRINT",EDGE,{"derivedFrom":sQuery(id+"F0.wireOp",EDGE,"E54.8")}),-1.0]])]});
            var Q4;
            Q4=makeQuery(id+"F0.imprint","IMPRINT",FACE,{"disambiguationData":[TD([[makeQuery(id+"F0.imprint","IMPRINT",EDGE,{"derivedFrom":sQuery(id+"F0.wireOp",EDGE,"E54.11")}),-1.0]])]});
            extrude(context, id + "F3", {"entities" : qUnion([Q0, Q1, Q2, Q3, Q4]), "operationType" : NewBodyOperationType.ADD, "depth" : 914.4 * mm, "offsetDistance" : 30.48 * mm});
        }
        {
            var Q0;
            Q0=makeQuery(id+"F0.imprint","IMPRINT",FACE,{"disambiguationData":[TD([[makeQuery(id+"F0.imprint","IMPRINT",EDGE,{"derivedFrom":sQuery(id+"F0.wireOp",EDGE,"E25.16")}),-1.0]])]});
            var Q1;
            {var subQ3=sQuery(id+"F0.wireOp",EDGE,"E25.13");Q1=makeQuery(id+"F0.imprint","IMPRINT",FACE,{"disambiguationData":[TD([[makeQuery(id+"F0.imprint","IMPRINT",EDGE,{"derivedFrom":subQ3}),-1.0]])]});}
            var Q2;
            Q2=makeQuery(id+"F0.imprint","IMPRINT",FACE,{"disambiguationData":[TD([[makeQuery(id+"F0.imprint","IMPRINT",EDGE,{"derivedFrom":sQuery(id+"F0.wireOp",EDGE,"E25.0")}),-1.0]])]});
            var Q3;
            Q3=makeQuery(id+"F0.imprint","IMPRINT",FACE,{"disambiguationData":[TD([[makeQuery(id+"F0.imprint","IMPRINT",EDGE,{"derivedFrom":sQuery(id+"F0.wireOp",EDGE,"E25.3")}),-1.0]])]});
            var Q4;
            Q4=makeQuery(id+"F0.imprint","IMPRINT",FACE,{"disambiguationData":[TD([[makeQuery(id+"F0.imprint","IMPRINT",EDGE,{"derivedFrom":sQuery(id+"F0.wireOp",EDGE,"E25.6")}),-1.0]])]});
            extrude(context, id + "F4", {"entities" : qUnion([Q0, Q1, Q2, Q3, Q4]), "operationType" : NewBodyOperationType.ADD, "depth" : 1219.2 * mm, "offsetDistance" : 30.48 * mm});
        }
        {
            var Q0;
            {var subQ2=sQuery(id+"F0.wireOp",EDGE,"E28.13");Q0=makeQuery(id+"F0.imprint","IMPRINT",FACE,{"disambiguationData":[TD([[makeQuery(id+"F0.imprint","IMPRINT",EDGE,{"derivedFrom":subQ2}),1.0]])]});}
            var Q1;
            Q1=makeQuery(id+"F0.imprint","IMPRINT",FACE,{"disambiguationData":[TD([[makeQuery(id+"F0.imprint","IMPRINT",EDGE,{"derivedFrom":sQuery(id+"F0.wireOp",EDGE,"E28.16")}),1.0]])]});
            var Q2;
            {var subQ9=sQuery(id+"F0.wireOp",EDGE,"E28.1");Q2=makeQuery(id+"F0.imprint","IMPRINT",FACE,{"disambiguationData":[TD([[makeQuery(id+"F0.imprint","IMPRINT",EDGE,{"derivedFrom":subQ9}),1.0]])]});}
            var Q3;
            Q3=makeQuery(id+"F0.imprint","IMPRINT",FACE,{"disambiguationData":[TD([[makeQuery(id+"F0.imprint","IMPRINT",EDGE,{"derivedFrom":sQuery(id+"F0.wireOp",EDGE,"E28.3")}),1.0]])]});
            var Q4;
            Q4=makeQuery(id+"F0.imprint","IMPRINT",FACE,{"disambiguationData":[TD([[makeQuery(id+"F0.imprint","IMPRINT",EDGE,{"derivedFrom":sQuery(id+"F0.wireOp",EDGE,"E28.6")}),1.0]])]});
            extrude(context, id + "F5", {"entities" : qUnion([Q0, Q1, Q2, Q3, Q4]), "operationType" : NewBodyOperationType.ADD, "depth" : 304.8 * mm, "offsetDistance" : 30.48 * mm});
        }
        {
            var Q0;
            Q0=makeQuery(id+"F0.imprint","IMPRINT",FACE,{"disambiguationData":[TD([[makeQuery(id+"F0.imprint","IMPRINT",EDGE,{"derivedFrom":sQuery(id+"F0.wireOp",EDGE,"E88")}),1.0]])]});
            var Q1;
            Q1=makeQuery(id+"F0.imprint","IMPRINT",FACE,{"disambiguationData":[TD([[makeQuery(id+"F0.imprint","IMPRINT",EDGE,{"derivedFrom":sQuery(id+"F0.wireOp",EDGE,"E89.19.0")}),1.0]])]});
            var Q2;
            Q2=makeQuery(id+"F0.imprint","IMPRINT",FACE,{"disambiguationData":[TD([[makeQuery(id+"F0.imprint","IMPRINT",EDGE,{"derivedFrom":sQuery(id+"F0.wireOp",EDGE,"E89.18.0")}),1.0]])]});
            var Q3;
            Q3=makeQuery(id+"F0.imprint","IMPRINT",FACE,{"disambiguationData":[TD([[makeQuery(id+"F0.imprint","IMPRINT",EDGE,{"derivedFrom":sQuery(id+"F0.wireOp",EDGE,"E89.17.0")}),1.0]])]});
            var Q4;
            Q4=makeQuery(id+"F0.imprint","IMPRINT",FACE,{"disambiguationData":[TD([[makeQuery(id+"F0.imprint","IMPRINT",EDGE,{"derivedFrom":sQuery(id+"F0.wireOp",EDGE,"E89.16.0")}),1.0]])]});
            var Q5;
            Q5=makeQuery(id+"F0.imprint","IMPRINT",FACE,{"disambiguationData":[TD([[makeQuery(id+"F0.imprint","IMPRINT",EDGE,{"derivedFrom":sQuery(id+"F0.wireOp",EDGE,"E89.15.0")}),1.0]])]});
            var Q6;
            Q6=makeQuery(id+"F0.imprint","IMPRINT",FACE,{"disambiguationData":[TD([[makeQuery(id+"F0.imprint","IMPRINT",EDGE,{"derivedFrom":sQuery(id+"F0.wireOp",EDGE,"E89.14.0")}),1.0]])]});
            var Q7;
            Q7=makeQuery(id+"F0.imprint","IMPRINT",FACE,{"disambiguationData":[TD([[makeQuery(id+"F0.imprint","IMPRINT",EDGE,{"derivedFrom":sQuery(id+"F0.wireOp",EDGE,"E89.13.0")}),1.0]])]});
            var Q8;
            Q8=makeQuery(id+"F0.imprint","IMPRINT",FACE,{"disambiguationData":[TD([[makeQuery(id+"F0.imprint","IMPRINT",EDGE,{"derivedFrom":sQuery(id+"F0.wireOp",EDGE,"E89.12.0")}),1.0]])]});
            var Q9;
            Q9=makeQuery(id+"F0.imprint","IMPRINT",FACE,{"disambiguationData":[TD([[makeQuery(id+"F0.imprint","IMPRINT",EDGE,{"derivedFrom":sQuery(id+"F0.wireOp",EDGE,"E89.11.0")}),1.0]])]});
            var Q10;
            Q10=makeQuery(id+"F0.imprint","IMPRINT",FACE,{"disambiguationData":[TD([[makeQuery(id+"F0.imprint","IMPRINT",EDGE,{"derivedFrom":sQuery(id+"F0.wireOp",EDGE,"E89.10.0")}),1.0]])]});
            var Q11;
            Q11=makeQuery(id+"F0.imprint","IMPRINT",FACE,{"disambiguationData":[TD([[makeQuery(id+"F0.imprint","IMPRINT",EDGE,{"derivedFrom":sQuery(id+"F0.wireOp",EDGE,"E89.9.0")}),1.0]])]});
            var Q12;
            Q12=makeQuery(id+"F0.imprint","IMPRINT",FACE,{"disambiguationData":[TD([[makeQuery(id+"F0.imprint","IMPRINT",EDGE,{"derivedFrom":sQuery(id+"F0.wireOp",EDGE,"E89.8.0")}),1.0]])]});
            var Q13;
            Q13=makeQuery(id+"F0.imprint","IMPRINT",FACE,{"disambiguationData":[TD([[makeQuery(id+"F0.imprint","IMPRINT",EDGE,{"derivedFrom":sQuery(id+"F0.wireOp",EDGE,"E89.7.0")}),1.0]])]});
            extrude(context, id + "F6", {"entities" : qUnion([Q0, Q1, Q2, Q3, Q4, Q5, Q6, Q7, Q8, Q9, Q10, Q11, Q12, Q13]), "operationType" : NewBodyOperationType.ADD, "depth" : 4724.4 * mm, "offsetDistance" : 30.48 * mm});
        }
        {
            var Q0;
            {var subQ1=sQuery(id+"F0.wireOp",EDGE,"E10");Q0=makeQuery(id+"F0.imprint","IMPRINT",FACE,{"disambiguationData":[TD([[makeQuery(id+"F0.imprint","IMPRINT",EDGE,{"derivedFrom":subQ1}),-1.0]])]});}
            var Q1;
            Q1=makeQuery(id+"F0.imprint","IMPRINT",FACE,{"disambiguationData":[TD([[makeQuery(id+"F0.imprint","IMPRINT",EDGE,{"derivedFrom":sQuery(id+"F0.wireOp",EDGE,"E19")}),-1.0]])]});
            var Q2;
            Q2=makeQuery(id+"F0.imprint","IMPRINT",FACE,{"disambiguationData":[TD([[makeQuery(id+"F0.imprint","IMPRINT",EDGE,{"derivedFrom":sQuery(id+"F0.wireOp",EDGE,"E76")}),1.0]])]});
            var Q3;
            Q3=makeQuery(id+"F0.imprint","IMPRINT",FACE,{"disambiguationData":[TD([[makeQuery(id+"F0.imprint","IMPRINT",EDGE,{"derivedFrom":sQuery(id+"F0.wireOp",EDGE,"E12")}),-1.0]])]});
            extrude(context, id + "F7", {"entities" : qUnion([Q0, Q1, Q2, Q3]), "operationType" : NewBodyOperationType.REMOVE, "depth" : 2438.4 * mm, "offsetDistance" : 30.48 * mm});
        }
    });
